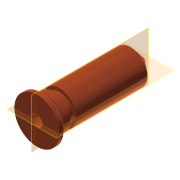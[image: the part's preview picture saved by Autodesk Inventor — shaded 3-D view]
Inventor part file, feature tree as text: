
AUTODESK INVENTOR PART (.ipt)
format: ipt  version: 2016 (Build 200138000, 138)  size: 174,592 bytes
history: native  units: mm
features: sketch x6, extrude x3, revolve x3, chamfer x1
ambient origin geometry x8: Origin, YZ Plane, XZ Plane, XY Plane, X Axis, Y Axis, Z Axis, Center Point
bodies: Solid1 (feature_tree)
feature tree (13):
  extrude  "Extrusion1"  Depth=1.0mm TaperAngle=0.0deg
  extrude  "Extrusion2"  Depth=15.584mm TaperAngle=0.0deg
  extrude  "Extrusion3"  Depth=2.0mm TaperAngle=0.0deg
  revolve  "Revolution1"  [1 undecoded]
  revolve  "Revolution2"  Angle=90.0deg
  chamfer  "Chamfer1"  Angle=90.0deg  [1 undecoded]
  revolve  "Revolution3"  Angle=45.0deg
  sketch  "Sketch1"  dims[d0=8.0mm d1=1.0mm d2=0.0mm]
  sketch  "Sketch2"  dims[d3=6.0mm d4=15.584mm d5=0.0mm]
  sketch  "Sketch3"  dims[d6=2.0mm d7=21.0mm d8=0.0mm]
  sketch  "Sketch4"  dims[d9=6.981317mm d10=0.2mm]
  sketch  "Sketch5"  dims[d11=30.0deg d13=90.0deg]
  sketch  "Sketch6"  dims[d14=0.7mm d15=90.0deg d16=0.3mm d17=2.0mm d18=45.0deg d19=45.0deg d20=0.05mm d21=0.3mm d22=0.05mm d23=0.6mm d24=1.0mm d25=3.0mm d26=90.0deg]
note: 2 required parameter values undecoded (feature->parameter linkage not recoverable at this tier; creation-order binding heuristic only, values carry confidence <= 0.55)